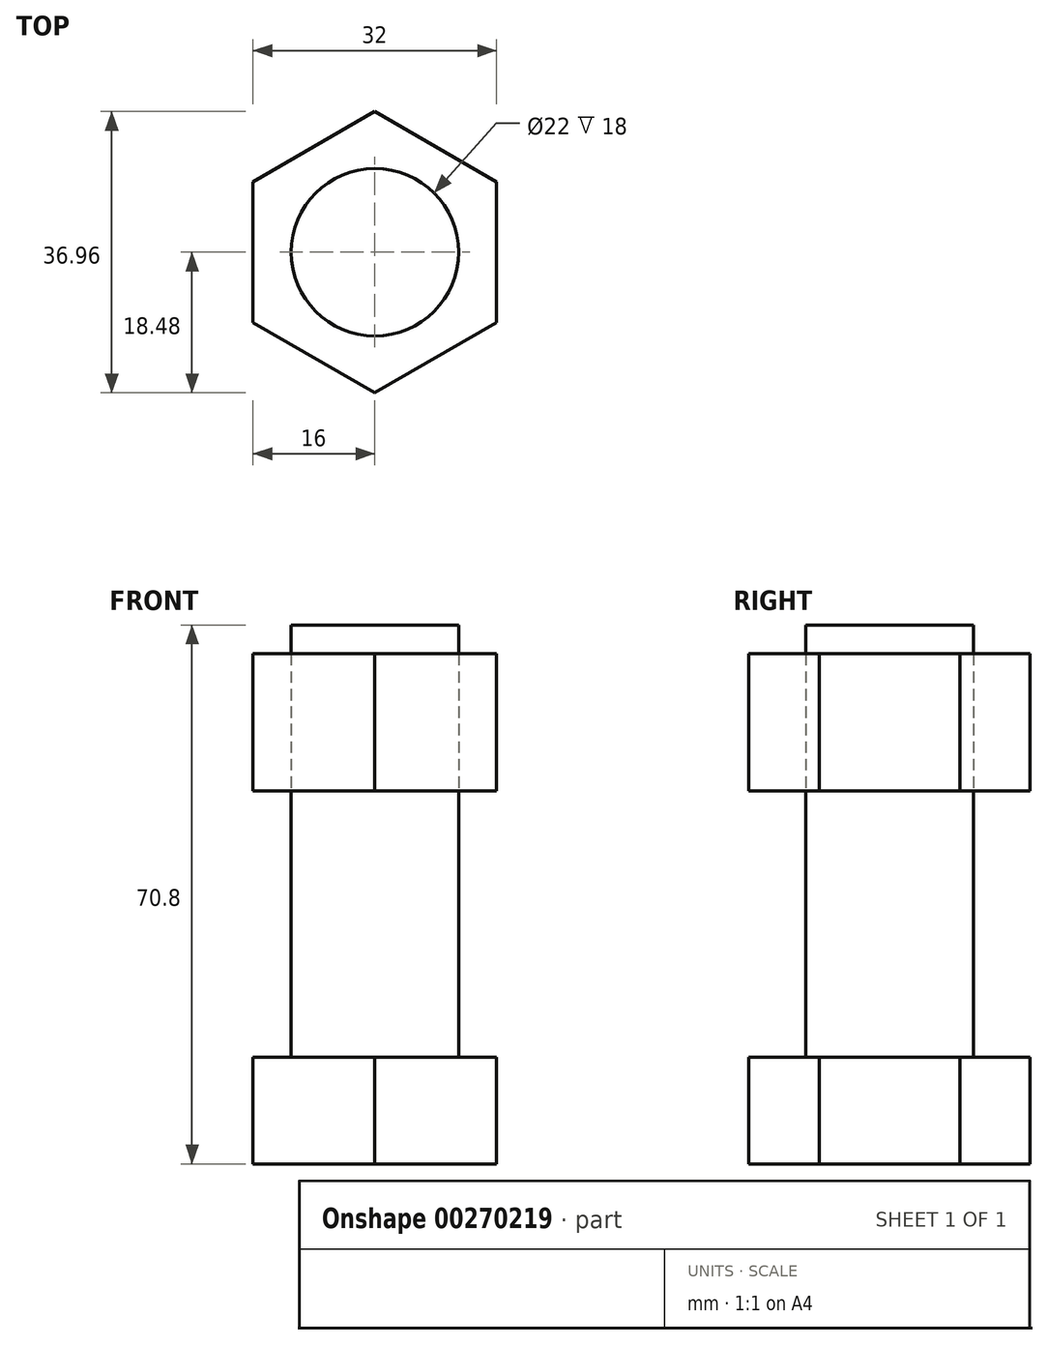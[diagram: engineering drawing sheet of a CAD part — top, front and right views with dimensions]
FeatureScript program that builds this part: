
annotation { "Feature Type Name" : "Feature", "Feature Type Description" : "" }
export const myFeature = defineFeature(function(context is Context, id is Id, definition is map)
    precondition{}
    {
        {
            var Q0;
            Q0=qCreatedBy(makeId("Top.planeOp"),FACE);
            var sketch = newSketch(context, id + "F0", { "sketchPlane" : qUnion([Q0])});
            skCircle(sketch, "E0.cCircle", {"center": v(0, 0) * mm, "radius": 16 * mm, "construction": true});
            skLineSegment(sketch, "E0.0", {"start": v(16, 9.24) * mm, "end": v(16, -9.24) * mm});
            skLineSegment(sketch, "E0.1", {"start": v(16, -9.24) * mm, "end": v(0, -18.48) * mm});
            skLineSegment(sketch, "E0.2", {"start": v(0, -18.48) * mm, "end": v(-16, -9.24) * mm});
            skLineSegment(sketch, "E0.3", {"start": v(-16, -9.24) * mm, "end": v(-16, 9.24) * mm});
            skLineSegment(sketch, "E0.4", {"start": v(-16, 9.24) * mm, "end": v(0, 18.48) * mm});
            skLineSegment(sketch, "E0.5", {"start": v(0, 18.48) * mm, "end": v(16, 9.24) * mm});
            skPoint(sketch, "E0.0.midPoint", {"position": v(16, 0) * mm});
            skSolve(sketch);
        }
        {
            var Q0;
            Q0=makeQuery(id+"F0.imprint","IMPRINT",FACE,{"disambiguationData":[TD([[makeQuery(id+"F0.imprint","IMPRINT",EDGE,{"derivedFrom":sQuery(id+"F0.wireOp",EDGE,"E0.0")}),-1.0]])]});
            extrude(context, id + "F1", {"entities" : qUnion([Q0]), "depth" : 14 * mm});
        }
        {
            var Q0;
            Q0=makeQuery(id+"F1.opExtrude","CAP_FACE",FACE,{"disambiguationData":[OSD([sQuery(id+"F0.wireOp",EDGE,"E0.0"),sQuery(id+"F0.wireOp",EDGE,"E0.1"),sQuery(id+"F0.wireOp",EDGE,"E0.2"),sQuery(id+"F0.wireOp",EDGE,"E0.3"),sQuery(id+"F0.wireOp",EDGE,"E0.4"),sQuery(id+"F0.wireOp",EDGE,"E0.5")])],"isStart":false});
            var sketch = newSketch(context, id + "F2", { "sketchPlane" : qUnion([Q0])});
            skCircle(sketch, "E1", {"center": v(0, 0) * mm, "radius": 11 * mm});
            skSolve(sketch);
        }
        {
            var Q0;
            Q0=makeQuery(id+"F2.imprint","IMPRINT",FACE,{"disambiguationData":[TD([[makeQuery(id+"F2.imprint","IMPRINT",EDGE,{"derivedFrom":sQuery(id+"F2.wireOp",EDGE,"E1")}),1.0]])]});
            extrude(context, id + "F3", {"entities" : qUnion([Q0]), "operationType" : NewBodyOperationType.ADD, "depth" : 35 * mm});
        }
        {
            var Q0;
            Q0=makeQuery(id+"F3.opExtrude","CAP_FACE",FACE,{"disambiguationData":[OSD([sQuery(id+"F2.wireOp",EDGE,"E1")])],"isStart":false});
            var sketch = newSketch(context, id + "F4", { "sketchPlane" : qUnion([Q0])});
            skCircle(sketch, "E2.cCircle", {"center": v(0, 0) * mm, "radius": 16 * mm, "construction": true});
            skLineSegment(sketch, "E2.0", {"start": v(16, 9.24) * mm, "end": v(16, -9.24) * mm});
            skLineSegment(sketch, "E2.1", {"start": v(16, -9.24) * mm, "end": v(0, -18.48) * mm});
            skLineSegment(sketch, "E2.2", {"start": v(0, -18.48) * mm, "end": v(-16, -9.24) * mm});
            skLineSegment(sketch, "E2.3", {"start": v(-16, -9.24) * mm, "end": v(-16, 9.24) * mm});
            skLineSegment(sketch, "E2.4", {"start": v(-16, 9.24) * mm, "end": v(0, 18.48) * mm});
            skLineSegment(sketch, "E2.5", {"start": v(0, 18.48) * mm, "end": v(16, 9.24) * mm});
            skPoint(sketch, "E2.0.midPoint", {"position": v(16, 0) * mm});
            skCircle(sketch, "E3", {"center": v(0, 0) * mm, "radius": 11 * mm});
            skSolve(sketch);
        }
        {
            var Q0;
            Q0=makeQuery(id+"F4.imprint","IMPRINT",FACE,{"disambiguationData":[TD([[makeQuery(id+"F4.imprint","IMPRINT",EDGE,{"derivedFrom":sQuery(id+"F4.wireOp",EDGE,"E2.0")}),-1.0]])]});
            extrude(context, id + "F5", {"entities" : qUnion([Q0]), "depth" : 18 * mm});
        }
        {
            var Q0;
            Q0=makeQuery(id+"F3.opExtrude","CAP_FACE",FACE,{"disambiguationData":[OSD([sQuery(id+"F2.wireOp",EDGE,"E1")])],"isStart":false});
            extrude(context, id + "F6", {"entities" : qUnion([Q0]), "depth" : 21.8 * mm});
        }
    });
